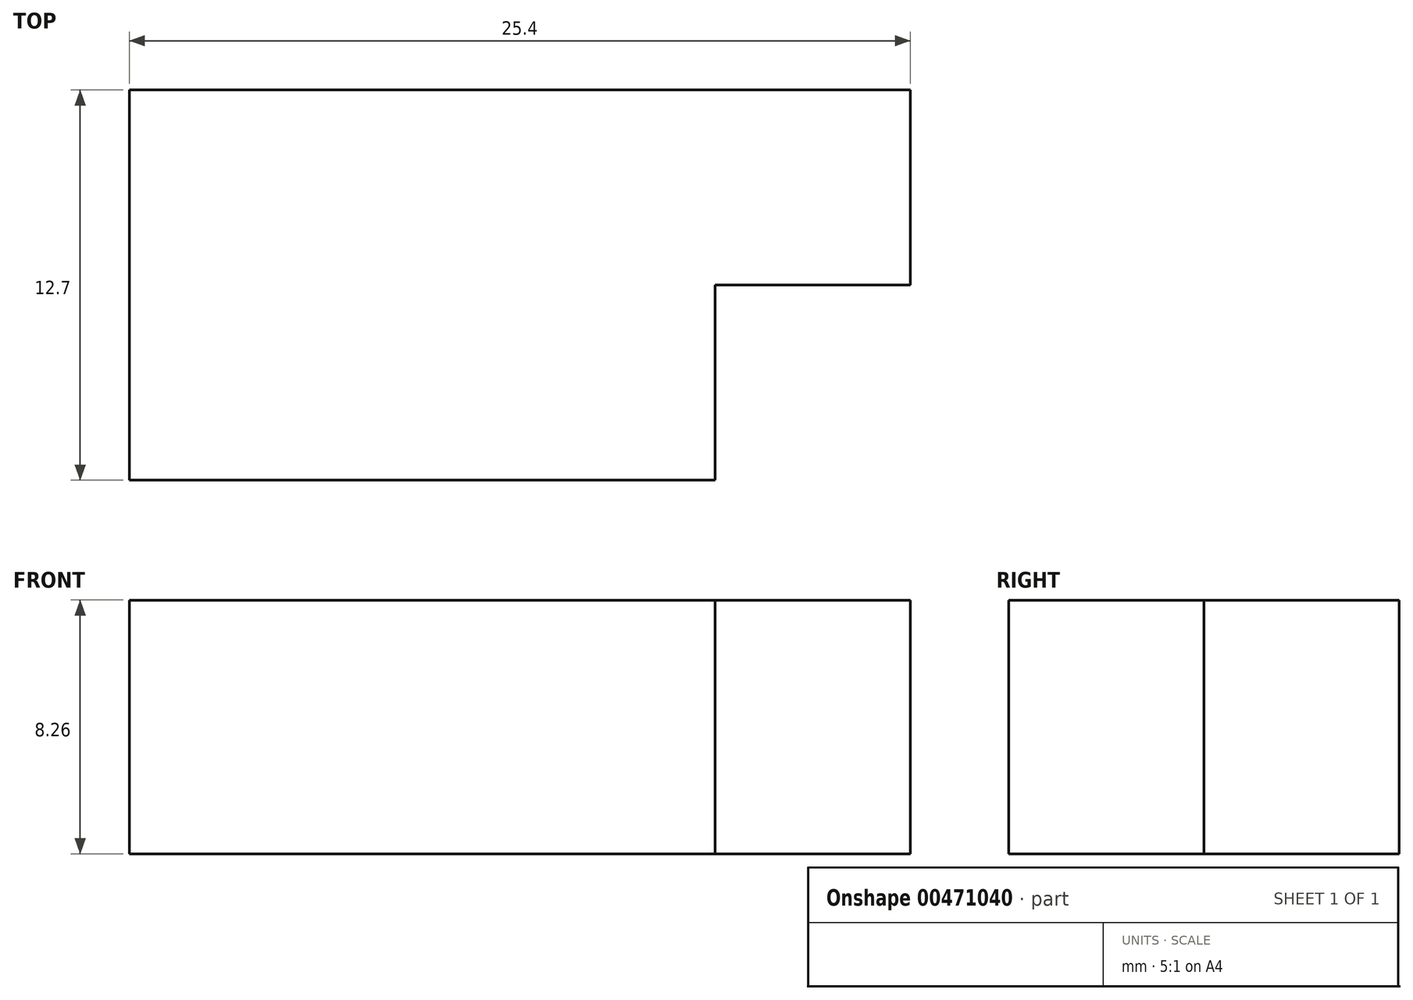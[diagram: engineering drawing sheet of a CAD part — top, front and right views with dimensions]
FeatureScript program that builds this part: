
annotation { "Feature Type Name" : "Feature", "Feature Type Description" : "" }
export const myFeature = defineFeature(function(context is Context, id is Id, definition is map)
    precondition{}
    {
        {
            var Q0;
            Q0=qCreatedBy(makeId("Top.planeOp"),FACE);
            var sketch = newSketch(context, id + "F0", { "sketchPlane" : qUnion([Q0])});
            skLineSegment(sketch, "E0", {"start": v(0, 0) * mm, "end": v(-19.05, 0) * mm});
            skLineSegment(sketch, "E1", {"start": v(-19.05, 0) * mm, "end": v(-19.05, 12.7) * mm});
            skLineSegment(sketch, "E2", {"start": v(-19.05, 12.7) * mm, "end": v(6.35, 12.7) * mm});
            skLineSegment(sketch, "E3", {"start": v(6.35, 12.7) * mm, "end": v(6.35, 6.35) * mm});
            skLineSegment(sketch, "E4", {"start": v(6.35, 6.35) * mm, "end": v(0, 6.35) * mm});
            skLineSegment(sketch, "E5", {"start": v(0, 6.35) * mm, "end": v(0, 0) * mm});
            skSolve(sketch);
        }
        {
            var Q0;
            Q0 = qSketchRegion(id + "F0", true);
            extrude(context, id + "F1", {"entities" : qUnion([Q0]), "depth" : 8.25 * mm});
        }
    });
